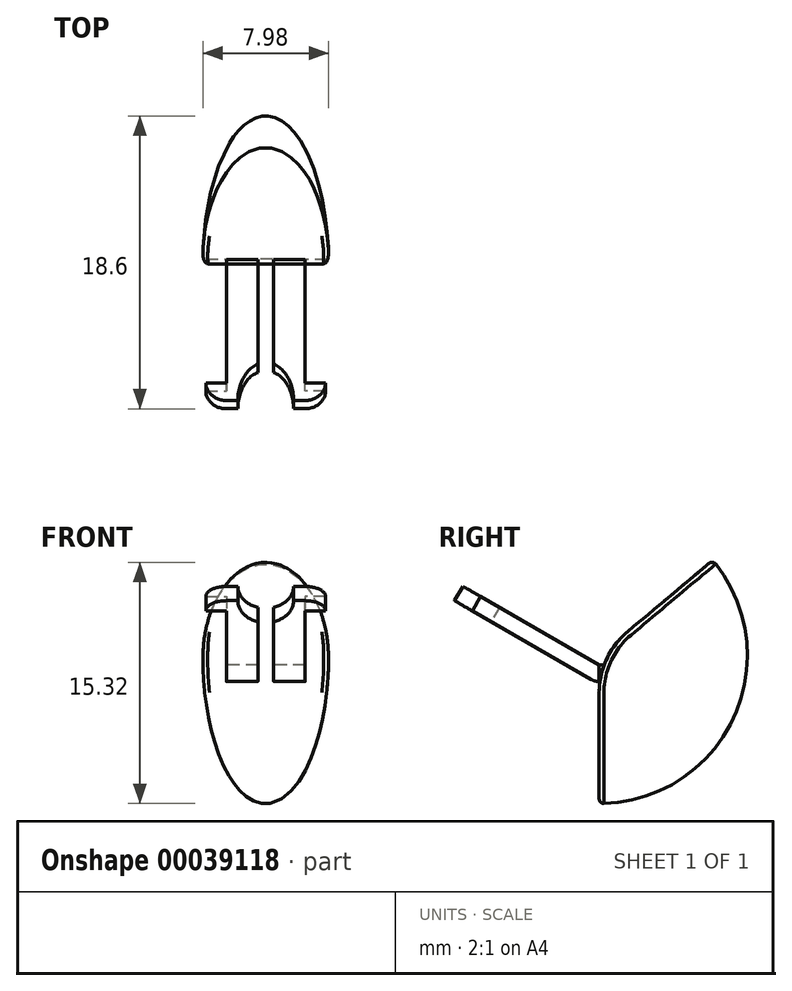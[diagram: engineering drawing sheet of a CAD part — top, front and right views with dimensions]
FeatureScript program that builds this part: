
annotation { "Feature Type Name" : "Feature", "Feature Type Description" : "" }
export const myFeature = defineFeature(function(context is Context, id is Id, definition is map)
    precondition{}
    {
        {
            var Q0;
            Q0=qCreatedBy(makeId("Front.planeOp"),FACE);
            var sketch = newSketch(context, id + "F0", { "sketchPlane" : qUnion([Q0])});
            skEllipticalArc(sketch, "E0", {});
            skLineSegment(sketch, "E1", {"start": v(0, 0) * mm, "end": v(4, 0) * mm});
            skLineSegment(sketch, "E2", {"start": v(4, 0) * mm, "end": v(0, 0) * mm});
            skLineSegment(sketch, "E3", {"start": v(-4, 0) * mm, "end": v(0, 0) * mm});
            skPoint(sketch, "E4.orphan", {"position": v(-15.94, 0) * mm});
            skLineSegment(sketch, "E5", {"start": v(4, 0) * mm, "end": v(12.84, 0) * mm});
            const initialGuessF0  = {"E0": [0, 0, 0, 1, 0.009408659280272449, 0.004, 1.5707963267948966, 4.71238898038469]};
            skSetInitialGuess(sketch, initialGuessF0);
            skSolve(sketch);
        }
        {
            var Q0;
            Q0 = qSketchRegion(id + "F0", true);
            var Q1;
            Q1=sQuery(id+"F0.wireOp",EDGE,"E1");
            revolve(context, id + "F1", {"entities" : qUnion([Q0]), "axis" : qUnion([Q1]), "revolveType" : RevolveType.ONE_DIRECTION, "angle" : 130 * degree});
        }
        {
            var Q0;
            Q0=makeQuery(id+"F1.opRevolve","CAP_EDGE",EDGE,{"disambiguationData":[OSD([sQuery(id+"F0.wireOp",EDGE,"E2"),sQuery(id+"F0.wireOp",EDGE,"E3")])],"isStart":true});
            fillet(context, id + "F2", {"entities" : qUnion([Q0]), "radius" : 5 * mm, "tangentPropagation" : true, "allowEdgeOverflow" : false});
        }
        {
            var Q0;
            Q0=makeQuery(id+"F1.opRevolve","CAP_EDGE",EDGE,{"disambiguationData":[OSD([sQuery(id+"F0.wireOp",EDGE,"E0")])],"isStart":false});
            fillet(context, id + "F3", {"entities" : qUnion([Q0]), "radius" : 0.3 * mm, "tangentPropagation" : true, "allowEdgeOverflow" : false});
        }
        {
            var Q0;
            Q0=makeQuery(id+"F1.opRevolve","CAP_FACE",FACE,{"disambiguationData":[OSD([sQuery(id+"F0.wireOp",EDGE,"E0"),sQuery(id+"F0.wireOp",EDGE,"E2"),sQuery(id+"F0.wireOp",EDGE,"E3")])],"isStart":true});
            var sketch = newSketch(context, id + "F4", { "sketchPlane" : qUnion([Q0])});
            skPoint(sketch, "E6", {"position": v(0, -9.1) * mm});
            skPoint(sketch, "E7", {"position": v(0, -2.33) * mm});
            skPoint(sketch, "E8", {"position": v(0, -1.13) * mm});
            skPoint(sketch, "E9", {"position": v(-1.5, -1.13) * mm});
            skPoint(sketch, "E10", {"position": v(1.5, -1.13) * mm});
            skLineSegment(sketch, "E11.rect.bottom", {"start": v(-0.5, -1.66) * mm, "end": v(-2.5, -1.66) * mm});
            skLineSegment(sketch, "E11.rect.top", {"start": v(-0.5, -0.6) * mm, "end": v(-2.5, -0.6) * mm});
            skLineSegment(sketch, "E11.rect.left", {"start": v(-0.5, -1.66) * mm, "end": v(-0.5, -0.6) * mm});
            skLineSegment(sketch, "E11.rect.right", {"start": v(-2.5, -1.66) * mm, "end": v(-2.5, -0.6) * mm});
            skLineSegment(sketch, "E12.rect.bottom", {"start": v(0.5, -0.6) * mm, "end": v(2.5, -0.6) * mm});
            skLineSegment(sketch, "E12.rect.top", {"start": v(0.5, -1.66) * mm, "end": v(2.5, -1.66) * mm});
            skLineSegment(sketch, "E12.rect.left", {"start": v(0.5, -0.6) * mm, "end": v(0.5, -1.66) * mm});
            skLineSegment(sketch, "E12.rect.right", {"start": v(2.5, -0.6) * mm, "end": v(2.5, -1.66) * mm});
            skSolve(sketch);
        }
        {
            var Q0;
            Q0 = qSketchRegion(id + "F4", true);
            var Q1;
            Q1=sQuery(id+"F4.wireOp",EDGE,"E11.rect.top");
            revolve(context, id + "F5", {"operationType" : NewBodyOperationType.ADD, "entities" : qUnion([Q0]), "axis" : qUnion([Q1]), "revolveType" : RevolveType.ONE_DIRECTION, "angle" : 30 * degree});
        }
        {
            var Q0;
            Q0=makeQuery(id+"F5.opRevolve","CAP_FACE",FACE,{"disambiguationData":[OSD([sQuery(id+"F4.wireOp",EDGE,"E11.rect.bottom"),sQuery(id+"F4.wireOp",EDGE,"E11.rect.top"),sQuery(id+"F4.wireOp",EDGE,"E11.rect.left"),sQuery(id+"F4.wireOp",EDGE,"E11.rect.right")])],"isStart":false});
            var Q1;
            Q1=makeQuery(id+"F5.opRevolve","CAP_FACE",FACE,{"disambiguationData":[OSD([sQuery(id+"F4.wireOp",EDGE,"E12.rect.bottom"),sQuery(id+"F4.wireOp",EDGE,"E12.rect.top"),sQuery(id+"F4.wireOp",EDGE,"E12.rect.left"),sQuery(id+"F4.wireOp",EDGE,"E12.rect.right")])],"isStart":false});
            extrude(context, id + "F6", {"entities" : qUnion([Q0, Q1]), "operationType" : NewBodyOperationType.ADD, "depth" : 10 * mm});
        }
        {
            var Q0;
            {var subQ0=sQuery(id+"F4.wireOp",EDGE,"E12.rect.right");Q0=makeQuery(id+"F6.boolean.opBoolean","MERGE",FACE,{"derivedFrom":[makeQuery(id+"F5.opRevolve","SWEPT_FACE",FACE,{"disambiguationData":[OSD([subQ0])]}),makeQuery(id+"F6.opExtrude","SWEPT_FACE",FACE,{"disambiguationData":[OSD([subQ0])]})]});}
            var sketch = newSketch(context, id + "F7", { "sketchPlane" : qUnion([Q0])});
            skLineSegment(sketch, "E13", {"start": v(-8.66, 4.4) * mm, "end": v(-9.19, 3.48) * mm});
            skLineSegment(sketch, "E14", {"start": v(-9.19, 3.48) * mm, "end": v(-8.06, 2.83) * mm});
            skLineSegment(sketch, "E15", {"start": v(-8.06, 2.83) * mm, "end": v(-7.53, 3.74) * mm});
            skLineSegment(sketch, "E16", {"start": v(-7.53, 3.74) * mm, "end": v(-8.66, 4.4) * mm});
            skSolve(sketch);
        }
        {
            var Q0;
            Q0 = qSketchRegion(id + "F7", true);
            var Q1;
            Q1=sQuery(id+"F7.wireOp",EDGE,"E15");
            revolve(context, id + "F8", {"operationType" : NewBodyOperationType.ADD, "entities" : qUnion([Q0]), "axis" : qUnion([Q1]), "revolveType" : RevolveType.ONE_DIRECTION, "angle" : 90 * degree});
        }
        {
            var Q0;
            {var subQ0=sQuery(id+"F4.wireOp",EDGE,"E11.rect.right");Q0=makeQuery(id+"F6.boolean.opBoolean","MERGE",FACE,{"derivedFrom":[makeQuery(id+"F5.opRevolve","SWEPT_FACE",FACE,{"disambiguationData":[OSD([subQ0])]}),makeQuery(id+"F6.opExtrude","SWEPT_FACE",FACE,{"disambiguationData":[OSD([subQ0])]})]});}
            var sketch = newSketch(context, id + "F9", { "sketchPlane" : qUnion([Q0])});
            skLineSegment(sketch, "E17", {"start": v(9.19, 3.48) * mm, "end": v(8.66, 4.4) * mm});
            skLineSegment(sketch, "E18", {"start": v(8.66, 4.4) * mm, "end": v(7.53, 3.74) * mm});
            skLineSegment(sketch, "E19", {"start": v(7.53, 3.74) * mm, "end": v(8.06, 2.83) * mm});
            skLineSegment(sketch, "E20", {"start": v(8.06, 2.83) * mm, "end": v(9.19, 3.48) * mm});
            skSolve(sketch);
        }
        {
            var Q0;
            Q0 = qSketchRegion(id + "F9", true);
            var Q1;
            Q1=sQuery(id+"F9.wireOp",EDGE,"E19");
            revolve(context, id + "F10", {"operationType" : NewBodyOperationType.ADD, "entities" : qUnion([Q0]), "axis" : qUnion([Q1]), "revolveType" : RevolveType.ONE_DIRECTION, "angle" : 90 * degree});
        }
        {
            var Q0;
            Q0=makeQuery(id+"F8.boolean.opBoolean","MERGE",FACE,{"derivedFrom":[makeQuery(id+"F6.opExtrude","SWEPT_FACE",FACE,{"disambiguationData":[OSD([sQuery(id+"F4.wireOp",EDGE,"E12.rect.top")])]}),makeQuery(id+"F8.opRevolve","SWEPT_FACE",FACE,{"disambiguationData":[OSD([sQuery(id+"F7.wireOp",EDGE,"E14")])]})]});
            var sketch = newSketch(context, id + "F11", { "sketchPlane" : qUnion([Q0])});
            skEllipse(sketch, "E21", {"center": v(0, 9.7) * mm, "majorRadius": 2.79 * mm, "minorRadius": 1.77 * mm, "majorAxis": v(0, 1)});
            skSolve(sketch);
        }
        {
            var Q0;
            Q0 = qSketchRegion(id + "F11", true);
            extrude(context, id + "F12", {"entities" : qUnion([Q0]), "operationType" : NewBodyOperationType.REMOVE, "oppositeDirection" : true, "depth" : 25 * mm});
        }
        {
            var Q0;
            Q0=makeQuery(id+"F5.opRevolve","CAP_FACE",FACE,{"disambiguationData":[OSD([sQuery(id+"F4.wireOp",EDGE,"E12.rect.bottom"),sQuery(id+"F4.wireOp",EDGE,"E12.rect.top"),sQuery(id+"F4.wireOp",EDGE,"E12.rect.left"),sQuery(id+"F4.wireOp",EDGE,"E12.rect.right")])],"isStart":true});
            extrude(context, id + "F13", {"entities" : qUnion([Q0]), "endBound" : BoundingType.UP_TO_NEXT, "depth" : 25 * mm});
        }
        {
            var Q0;
            Q0=makeQuery(id+"F5.opRevolve","CAP_FACE",FACE,{"disambiguationData":[OSD([sQuery(id+"F4.wireOp",EDGE,"E11.rect.bottom"),sQuery(id+"F4.wireOp",EDGE,"E11.rect.top"),sQuery(id+"F4.wireOp",EDGE,"E11.rect.left"),sQuery(id+"F4.wireOp",EDGE,"E11.rect.right")])],"isStart":true});
            extrude(context, id + "F14", {"entities" : qUnion([Q0]), "endBound" : BoundingType.UP_TO_NEXT, "depth" : 25 * mm});
        }
    });
